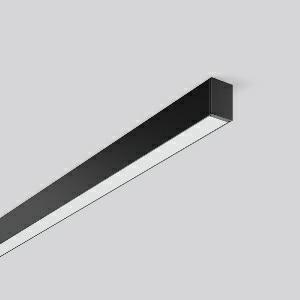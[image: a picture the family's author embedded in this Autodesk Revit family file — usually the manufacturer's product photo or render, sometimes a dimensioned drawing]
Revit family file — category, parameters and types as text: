
# Revit family: less_is_more_27_312201_003_1_76_e40e
name_source: partatom
category: Lighting Fixtures
units: mm (PartAtom-declared; Revit-internal decimal feet)

## family parameters
Cut with Voids When Loaded = No
Host = Face
Light Source = No
Part Type = Normal
Room Calculation Point = No
Round Connector Dimension = Use Diameter
Shared = No

## types (1)
- LESS IS MORE 27 (1 x LED Modul 840, 2750 lm, 4000)
    Apparent Load = 39 VA
    CIE Flux Codes = 65 89 98 100 100
    Color Rendering = 80
    Color Temperature = 4000
    Default Elevation = 1800 mm
    Description = Series: LESS IS MORE 27
Ceiling luminaire with slim design. Housing: extruded aluminium profile, powder-coated. End cap aluminium powder-coated. Diffuser made of non-yellowing plastic (PMMA) microprismatic. Suitable for Ceiling mounting, Wall (surface). External driver with connecting cable. 
Colour: deep black, matt (RAL 9005)
Length: 1512 mm
Width: 28 mm
Height: 38 mm
Lamp: LED
Socket: without socket
Colour temperature: 4000K
Colour rendering index (CRI): 82
System power: 39 W
Rated luminous flux: 2750 lm
Luminous efficiency: 71 lm/W
Control gear: Voltage converter, DALI dim.
Protection class: II
Type of protection: IP 20
    Height = 38 mm
    Lamp = 1 x LED Modul 840
    Lamp Light Flux = 2750 lm
    Lamp count = 1
    Length = 1512 mm
    Lifetime = 50000 h
    Luminous efficacy = 71 lm/W
    Manufacturer = RZB
    ModVariant = No
    Model = 312201.003.1.76
    Mounting Place = Ceiling, Wall
    Mounting Type = Surface mounted
    Number of Poles = 1
    OnlyDefault = Yes
    Power Factor = 1
    Product Name = LESS IS MORE 27
    Product group = Surface mounted LED linear luminaires
    ProductGroupID = 307
    Protection Class = Protection class II
    Protection Degree = IP 20
    RLX_Detail_Level = 1
    RLX_Emergency_Light_Flux = 0 lm
    RLX_Emergency_Type = 0
    RLX_Emergency_Type_DB = No
    RlxData = <blob elided: 29861 chars, md5=20d9391b>
    Socket = socket
    Standby Power = 0 W
    System Light Flux = 2750 lm
    System Power = 39 W
    Type Comments = Product without accessories
    Type Image = 312196.003.jpg
    URL = http://relux.com
    VarID = ---
    Voltage = 230 V
    Voltage Range = 220-240 V
    Weight = 0.00 kg
    Width = 28 mm

## geometry (parser evidence)
native form markers: Blend x4, Sweep x10
no freeform markers — native parametric forms only
